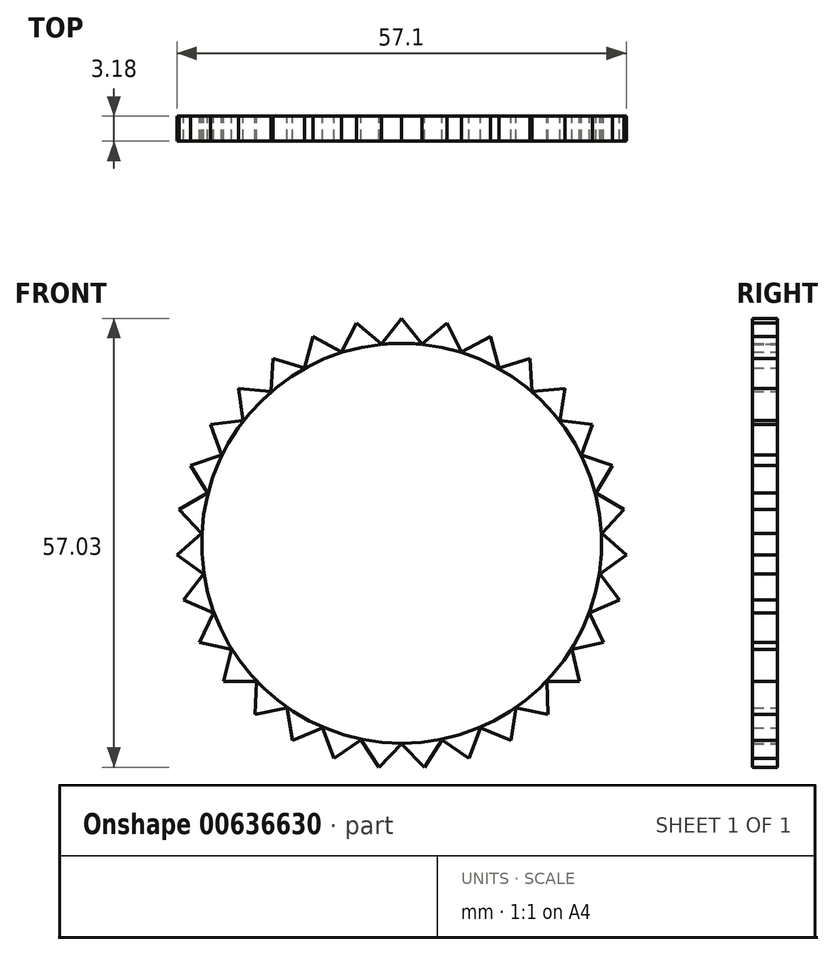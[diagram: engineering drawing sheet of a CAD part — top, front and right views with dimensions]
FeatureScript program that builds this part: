
annotation { "Feature Type Name" : "Feature", "Feature Type Description" : "" }
export const myFeature = defineFeature(function(context is Context, id is Id, definition is map)
    precondition{}
    {
        {
            var Q0;
            Q0=qCreatedBy(makeId("Front.planeOp"),FACE);
            var sketch = newSketch(context, id + "F0", { "sketchPlane" : qUnion([Q0])});
            skCircle(sketch, "E0", {"center": v(0, 0.01) * mm, "radius": 25.4 * mm});
            skLineSegment(sketch, "E1", {"start": v(0, 25.41) * mm, "end": v(0, 28.59) * mm});
            skLineSegment(sketch, "E2", {"start": v(0, 28.59) * mm, "end": v(-2.62, 25.28) * mm});
            skLineSegment(sketch, "E3.MirrorCS", {"start": v(0, 28.59) * mm, "end": v(2.62, 25.28) * mm});
            skLineSegment(sketch, "E4.1.0", {"start": v(-5.76, 28) * mm, "end": v(-7.66, 24.23) * mm});
            skLineSegment(sketch, "E4.1.1", {"start": v(-5.76, 28) * mm, "end": v(-2.52, 25.29) * mm});
            skLineSegment(sketch, "E4.2.0", {"start": v(-11.27, 26.27) * mm, "end": v(-12.38, 22.2) * mm});
            skLineSegment(sketch, "E4.2.1", {"start": v(-11.27, 26.27) * mm, "end": v(-7.56, 24.27) * mm});
            skLineSegment(sketch, "E4.3.0", {"start": v(-16.33, 23.47) * mm, "end": v(-16.6, 19.25) * mm});
            skLineSegment(sketch, "E4.3.1", {"start": v(-16.33, 23.47) * mm, "end": v(-12.29, 22.25) * mm});
            skLineSegment(sketch, "E4.4.0", {"start": v(-20.72, 19.7) * mm, "end": v(-20.13, 15.51) * mm});
            skLineSegment(sketch, "E4.4.1", {"start": v(-20.72, 19.7) * mm, "end": v(-16.51, 19.32) * mm});
            skLineSegment(sketch, "E4.5.0", {"start": v(-24.26, 15.12) * mm, "end": v(-22.84, 11.14) * mm});
            skLineSegment(sketch, "E4.5.1", {"start": v(-24.26, 15.12) * mm, "end": v(-20.06, 15.6) * mm});
            skLineSegment(sketch, "E4.6.0", {"start": v(-26.81, 9.93) * mm, "end": v(-24.62, 6.32) * mm});
            skLineSegment(sketch, "E4.6.1", {"start": v(-26.81, 9.93) * mm, "end": v(-22.8, 11.24) * mm});
            skLineSegment(sketch, "E4.7.0", {"start": v(-28.26, 4.33) * mm, "end": v(-25.38, 1.23) * mm});
            skLineSegment(sketch, "E4.7.1", {"start": v(-28.26, 4.33) * mm, "end": v(-24.59, 6.42) * mm});
            skLineSegment(sketch, "E4.8.0", {"start": v(-28.55, -1.45) * mm, "end": v(-25.11, -3.9) * mm});
            skLineSegment(sketch, "E4.8.1", {"start": v(-28.55, -1.45) * mm, "end": v(-25.38, 1.34) * mm});
            skLineSegment(sketch, "E4.9.0", {"start": v(-27.68, -7.17) * mm, "end": v(-23.81, -8.88) * mm});
            skLineSegment(sketch, "E4.9.1", {"start": v(-27.68, -7.17) * mm, "end": v(-25.13, -3.8) * mm});
            skLineSegment(sketch, "E4.10.0", {"start": v(-25.67, -12.6) * mm, "end": v(-21.54, -13.49) * mm});
            skLineSegment(sketch, "E4.10.1", {"start": v(-25.67, -12.6) * mm, "end": v(-23.85, -8.78) * mm});
            skLineSegment(sketch, "E4.11.0", {"start": v(-22.6, -17.5) * mm, "end": v(-18.38, -17.55) * mm});
            skLineSegment(sketch, "E4.11.1", {"start": v(-22.6, -17.5) * mm, "end": v(-21.6, -13.4) * mm});
            skLineSegment(sketch, "E4.12.0", {"start": v(-18.62, -21.7) * mm, "end": v(-14.47, -20.9) * mm});
            skLineSegment(sketch, "E4.12.1", {"start": v(-18.62, -21.7) * mm, "end": v(-18.46, -17.47) * mm});
            skLineSegment(sketch, "E4.13.0", {"start": v(-13.87, -25) * mm, "end": v(-9.97, -23.38) * mm});
            skLineSegment(sketch, "E4.13.1", {"start": v(-13.87, -25) * mm, "end": v(-14.56, -20.83) * mm});
            skLineSegment(sketch, "E4.14.0", {"start": v(-8.56, -27.28) * mm, "end": v(-5.06, -24.9) * mm});
            skLineSegment(sketch, "E4.14.1", {"start": v(-8.56, -27.28) * mm, "end": v(-10.07, -23.33) * mm});
            skLineSegment(sketch, "E4.15.0", {"start": v(-2.9, -28.44) * mm, "end": v(0.05, -25.41) * mm});
            skLineSegment(sketch, "E4.15.1", {"start": v(-2.9, -28.44) * mm, "end": v(-5.17, -24.88) * mm});
            skLineSegment(sketch, "E4.16.0", {"start": v(2.9, -28.44) * mm, "end": v(5.17, -24.88) * mm});
            skLineSegment(sketch, "E4.16.1", {"start": v(2.9, -28.44) * mm, "end": v(-0.05, -25.41) * mm});
            skLineSegment(sketch, "E4.17.0", {"start": v(8.56, -27.28) * mm, "end": v(10.07, -23.33) * mm});
            skLineSegment(sketch, "E4.17.1", {"start": v(8.56, -27.28) * mm, "end": v(5.06, -24.9) * mm});
            skLineSegment(sketch, "E4.18.0", {"start": v(13.87, -25) * mm, "end": v(14.56, -20.83) * mm});
            skLineSegment(sketch, "E4.18.1", {"start": v(13.87, -25) * mm, "end": v(9.97, -23.38) * mm});
            skLineSegment(sketch, "E4.19.0", {"start": v(18.62, -21.7) * mm, "end": v(18.46, -17.47) * mm});
            skLineSegment(sketch, "E4.19.1", {"start": v(18.62, -21.7) * mm, "end": v(14.47, -20.9) * mm});
            skLineSegment(sketch, "E4.20.0", {"start": v(22.6, -17.5) * mm, "end": v(21.6, -13.4) * mm});
            skLineSegment(sketch, "E4.20.1", {"start": v(22.6, -17.5) * mm, "end": v(18.38, -17.55) * mm});
            skLineSegment(sketch, "E4.21.0", {"start": v(25.67, -12.6) * mm, "end": v(23.85, -8.78) * mm});
            skLineSegment(sketch, "E4.21.1", {"start": v(25.67, -12.6) * mm, "end": v(21.54, -13.49) * mm});
            skLineSegment(sketch, "E4.22.0", {"start": v(27.68, -7.17) * mm, "end": v(25.13, -3.8) * mm});
            skLineSegment(sketch, "E4.22.1", {"start": v(27.68, -7.17) * mm, "end": v(23.81, -8.88) * mm});
            skLineSegment(sketch, "E4.23.0", {"start": v(28.55, -1.45) * mm, "end": v(25.38, 1.34) * mm});
            skLineSegment(sketch, "E4.23.1", {"start": v(28.55, -1.45) * mm, "end": v(25.11, -3.9) * mm});
            skLineSegment(sketch, "E4.24.0", {"start": v(28.26, 4.33) * mm, "end": v(24.59, 6.42) * mm});
            skLineSegment(sketch, "E4.24.1", {"start": v(28.26, 4.33) * mm, "end": v(25.38, 1.23) * mm});
            skLineSegment(sketch, "E4.25.0", {"start": v(26.81, 9.93) * mm, "end": v(22.8, 11.24) * mm});
            skLineSegment(sketch, "E4.25.1", {"start": v(26.81, 9.93) * mm, "end": v(24.62, 6.32) * mm});
            skLineSegment(sketch, "E4.26.0", {"start": v(24.26, 15.12) * mm, "end": v(20.06, 15.6) * mm});
            skLineSegment(sketch, "E4.26.1", {"start": v(24.26, 15.12) * mm, "end": v(22.84, 11.14) * mm});
            skLineSegment(sketch, "E4.27.0", {"start": v(20.72, 19.7) * mm, "end": v(16.51, 19.32) * mm});
            skLineSegment(sketch, "E4.27.1", {"start": v(20.72, 19.7) * mm, "end": v(20.13, 15.51) * mm});
            skLineSegment(sketch, "E4.28.0", {"start": v(16.33, 23.47) * mm, "end": v(12.29, 22.25) * mm});
            skLineSegment(sketch, "E4.28.1", {"start": v(16.33, 23.47) * mm, "end": v(16.6, 19.25) * mm});
            skLineSegment(sketch, "E4.29.0", {"start": v(11.27, 26.27) * mm, "end": v(7.56, 24.27) * mm});
            skLineSegment(sketch, "E4.29.1", {"start": v(11.27, 26.27) * mm, "end": v(12.38, 22.2) * mm});
            skPoint(sketch, "E4.center", {"position": v(0, 0) * mm});
            skLineSegment(sketch, "E5.2.30.0", {"start": v(5.76, 28) * mm, "end": v(2.52, 25.29) * mm});
            skLineSegment(sketch, "E5.3.30.0", {"start": v(5.76, 28) * mm, "end": v(7.66, 24.23) * mm});
            skSolve(sketch);
        }
        {
            var Q0;
            {var subQ0=sQuery(id+"F0.wireOp",EDGE,"E1");Q0=makeQuery(id+"F0.imprint","IMPRINT",FACE,{"disambiguationData":[TD([[makeQuery(id+"F0.imprint","IMPRINT",EDGE,{"derivedFrom":subQ0}),1.0]])]});}
            var Q1;
            {var subQ0=sQuery(id+"F0.wireOp",EDGE,"E1");Q1=makeQuery(id+"F0.imprint","IMPRINT",FACE,{"disambiguationData":[TD([[makeQuery(id+"F0.imprint","IMPRINT",EDGE,{"derivedFrom":subQ0}),-1.0]])]});}
            var Q2;
            {var subQ70=sQuery(id+"F0.wireOp",EDGE,"E2");var subQ74=sQuery(id+"F0.wireOp",EDGE,"E0");var subQ75=makeQuery(id+"F0.imprint","INTERSECT",VERTEX,{"derivedFrom":[subQ74,subQ70]});Q2=makeQuery(id+"F0.imprint","IMPRINT",FACE,{"disambiguationData":[TD([[makeQuery(id+"F0.imprint","IMPRINT",EDGE,{"disambiguationData":[TD([[subQ75,-1.0]])],"derivedFrom":subQ74}),-1.0]])]});}
            extrude(context, id + "F1", {"entities" : qUnion([Q0, Q1, Q2]), "depth" : 3.17 * mm, "offsetDistance" : 25.4 * mm});
        }
    });
